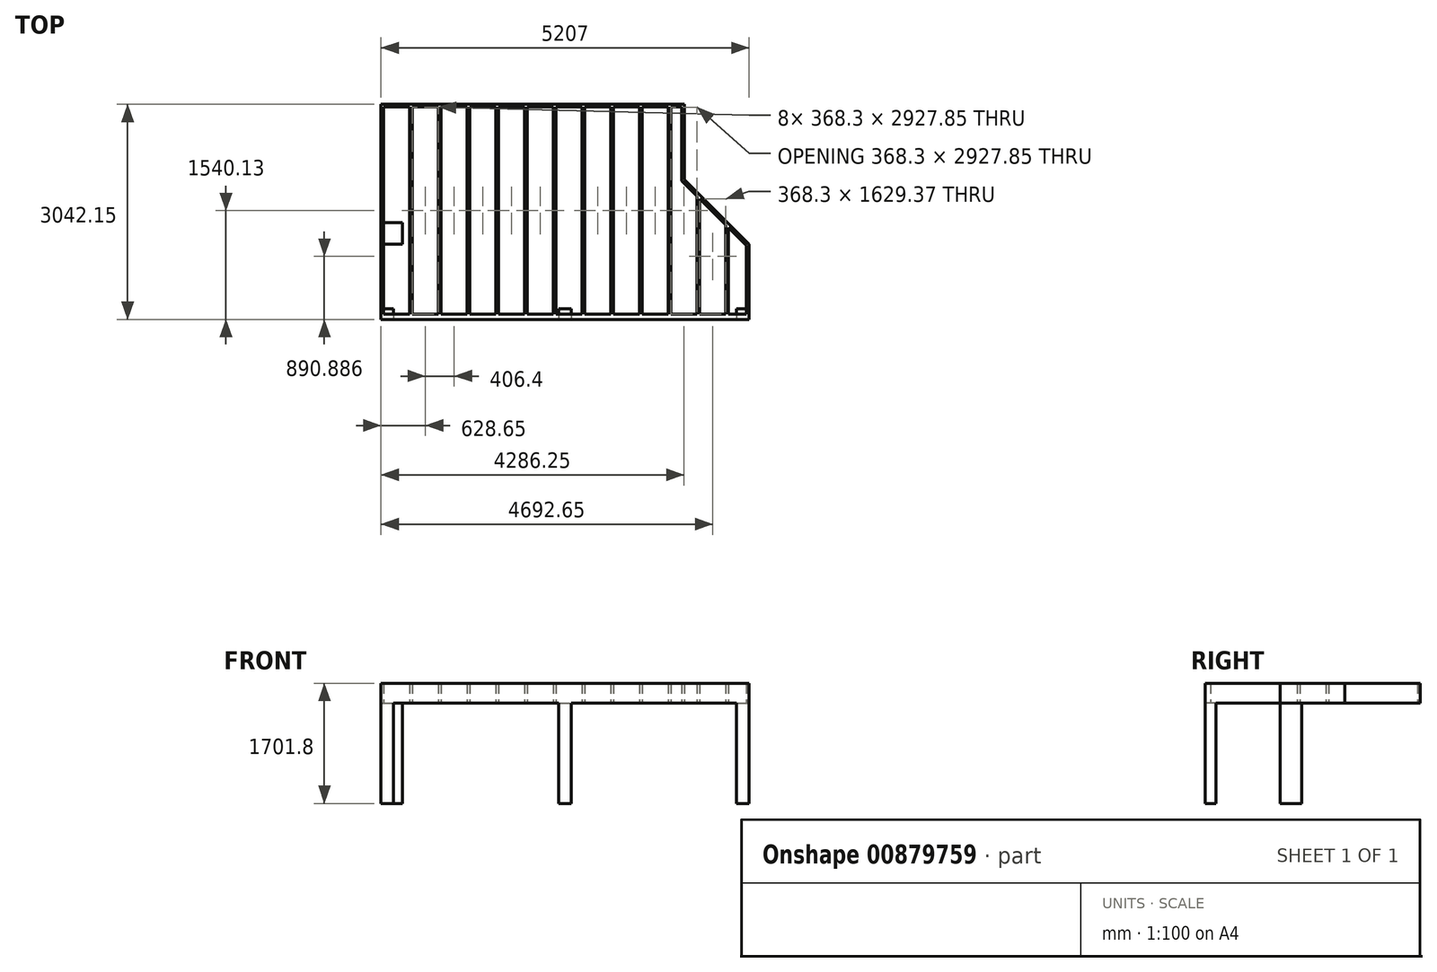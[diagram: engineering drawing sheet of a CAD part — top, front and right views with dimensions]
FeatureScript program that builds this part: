
annotation { "Feature Type Name" : "Feature", "Feature Type Description" : "" }
export const myFeature = defineFeature(function(context is Context, id is Id, definition is map)
    precondition{}
    {
        {
            var Q0;
            Q0=qCreatedBy(makeId("Top.planeOp"),FACE);
            var sketch = newSketch(context, id + "F0", { "sketchPlane" : qUnion([Q0])});
            skLineSegment(sketch, "E0.bottom", {"start": v(0, -1676.4) * mm, "end": v(304.8, -1676.4) * mm});
            skLineSegment(sketch, "E0.top", {"start": v(0, -1981.2) * mm, "end": v(304.8, -1981.2) * mm});
            skLineSegment(sketch, "E0.left", {"start": v(0, -1676.4) * mm, "end": v(0, -1981.2) * mm});
            skLineSegment(sketch, "E0.right", {"start": v(304.8, -1676.4) * mm, "end": v(304.8, -1981.2) * mm});
            skLineSegment(sketch, "E1.bottom", {"start": v(0, -2889.75) * mm, "end": v(177.8, -2889.75) * mm});
            skLineSegment(sketch, "E1.top", {"start": v(0, -3042.15) * mm, "end": v(177.8, -3042.15) * mm});
            skLineSegment(sketch, "E1.left", {"start": v(0, -2889.75) * mm, "end": v(0, -3042.15) * mm});
            skLineSegment(sketch, "E1.right", {"start": v(177.8, -2889.75) * mm, "end": v(177.8, -3042.15) * mm});
            skLineSegment(sketch, "E2.bottom", {"start": v(2514.6, -2889.75) * mm, "end": v(2692.4, -2889.75) * mm});
            skLineSegment(sketch, "E2.top", {"start": v(2514.6, -3042.15) * mm, "end": v(2692.4, -3042.15) * mm});
            skLineSegment(sketch, "E2.left", {"start": v(2514.6, -2889.75) * mm, "end": v(2514.6, -3042.15) * mm});
            skLineSegment(sketch, "E2.right", {"start": v(2692.4, -2889.75) * mm, "end": v(2692.4, -3042.15) * mm});
            skLineSegment(sketch, "E3.bottom", {"start": v(5029.2, -2889.75) * mm, "end": v(5207, -2889.75) * mm});
            skLineSegment(sketch, "E3.top", {"start": v(5029.2, -3042.15) * mm, "end": v(5207, -3042.15) * mm});
            skLineSegment(sketch, "E3.left", {"start": v(5029.2, -2889.75) * mm, "end": v(5029.2, -3042.15) * mm});
            skLineSegment(sketch, "E3.right", {"start": v(5207, -2889.75) * mm, "end": v(5207, -3042.15) * mm});
            skLineSegment(sketch, "E4", {"start": v(0, 0) * mm, "end": v(4292.6, 0) * mm, "construction": true});
            skLineSegment(sketch, "E5", {"start": v(4292.6, 0) * mm, "end": v(4292.6, -1066.8) * mm, "construction": true});
            skLineSegment(sketch, "E6", {"start": v(4292.6, -1066.8) * mm, "end": v(5226.55, -2000.75) * mm, "construction": true});
            skLineSegment(sketch, "E7", {"start": v(5226.55, -2000.75) * mm, "end": v(7106.15, -2000.75) * mm, "construction": true});
            skSolve(sketch);
        }
        {
            var Q0;
            Q0=qSketchRegion(id+"F0",true);
            extrude(context, id + "F1", {"entities" : qUnion([Q0]), "depth" : 1422.4 * mm, "offsetDistance" : 25.4 * mm});
        }
        {
            var Q0;
            Q0=makeQuery(id+"F1.opExtrude","CAP_FACE",FACE,{"disambiguationData":[OSD([sQuery(id+"F0.wireOp",EDGE,"E0.bottom"),sQuery(id+"F0.wireOp",EDGE,"E0.top"),sQuery(id+"F0.wireOp",EDGE,"E0.left"),sQuery(id+"F0.wireOp",EDGE,"E0.right")])],"isStart":false});
            var sketch = newSketch(context, id + "F2", { "sketchPlane" : qUnion([Q0])});
            skLineSegment(sketch, "E8.0", {"start": v(0, 0) * mm, "end": v(4292.6, 0) * mm});
            skLineSegment(sketch, "E9.0", {"start": v(4292.6, 0) * mm, "end": v(4292.6, -1066.8) * mm});
            skLineSegment(sketch, "E9.1", {"start": v(4292.6, -1066.8) * mm, "end": v(5207, -1981.2) * mm});
            skLineSegment(sketch, "E10", {"start": v(0, 0) * mm, "end": v(0, -3042.15) * mm});
            skLineSegment(sketch, "E11", {"start": v(0, -3042.15) * mm, "end": v(5207, -3042.15) * mm});
            skLineSegment(sketch, "E12", {"start": v(5207, -3042.15) * mm, "end": v(5207, -1981.2) * mm});
            skPoint(sketch, "E13.orphan", {"position": v(5226.55, -2000.75) * mm});
            skLineSegment(sketch, "E14.0", {"start": v(4254.5, -38.1) * mm, "end": v(4254.5, -1082.58) * mm});
            skLineSegment(sketch, "E14.1", {"start": v(5168.9, -3004.05) * mm, "end": v(5168.9, -1996.98) * mm});
            skLineSegment(sketch, "E14.2", {"start": v(38.1, -3004.05) * mm, "end": v(5168.9, -3004.05) * mm});
            skLineSegment(sketch, "E14.3", {"start": v(4254.5, -1082.58) * mm, "end": v(5168.9, -1996.98) * mm});
            skLineSegment(sketch, "E14.4", {"start": v(38.1, -38.1) * mm, "end": v(38.1, -3004.05) * mm});
            skLineSegment(sketch, "E14.5", {"start": v(38.1, -38.1) * mm, "end": v(4254.5, -38.1) * mm});
            skSolve(sketch);
        }
        {
            var Q0;
            Q0=qSketchRegion(id+"F2",true);
            extrude(context, id + "F3", {"entities" : qUnion([Q0]), "operationType" : NewBodyOperationType.ADD, "depth" : 279.4 * mm, "offsetDistance" : 25.4 * mm});
        }
        {
            var Q0;
            Q0=makeQuery(id+"F1.opExtrude","CAP_FACE",FACE,{"disambiguationData":[OSD([sQuery(id+"F0.wireOp",EDGE,"E1.bottom"),sQuery(id+"F0.wireOp",EDGE,"E1.top"),sQuery(id+"F0.wireOp",EDGE,"E1.left"),sQuery(id+"F0.wireOp",EDGE,"E1.right")])],"isStart":false});
            var sketch = newSketch(context, id + "F4", { "sketchPlane" : qUnion([Q0])});
            skPoint(sketch, "E15.oppositeSnap0", {"position": v(38.1, -2965.95) * mm});
            skLineSegment(sketch, "E15.bottom", {"start": v(38.1, -3004.05) * mm, "end": v(5168.9, -3004.05) * mm});
            skLineSegment(sketch, "E15.top", {"start": v(38.1, -2965.95) * mm, "end": v(5168.9, -2965.95) * mm});
            skLineSegment(sketch, "E15.left", {"start": v(38.1, -3004.05) * mm, "end": v(38.1, -2965.95) * mm});
            skLineSegment(sketch, "E15.right", {"start": v(5168.9, -3004.05) * mm, "end": v(5168.9, -2965.95) * mm});
            skSolve(sketch);
        }
        {
            var Q0;
            Q0=qSketchRegion(id+"F4",true);
            var Q1;
            Q1=makeQuery(id+"F3.opExtrude","CAP_FACE",FACE,{"disambiguationData":[OSD([sQuery(id+"F2.wireOp",EDGE,"E8.0"),sQuery(id+"F2.wireOp",EDGE,"E9.0"),sQuery(id+"F2.wireOp",EDGE,"E9.1"),sQuery(id+"F2.wireOp",EDGE,"E10"),sQuery(id+"F2.wireOp",EDGE,"E11"),sQuery(id+"F2.wireOp",EDGE,"E12"),sQuery(id+"F2.wireOp",EDGE,"E14.0"),sQuery(id+"F2.wireOp",EDGE,"E14.1"),sQuery(id+"F2.wireOp",EDGE,"E14.2"),sQuery(id+"F2.wireOp",EDGE,"E14.3"),sQuery(id+"F2.wireOp",EDGE,"E14.4"),sQuery(id+"F2.wireOp",EDGE,"E14.5")])],"isStart":false});
            extrude(context, id + "F5", {"entities" : qUnion([Q0]), "operationType" : NewBodyOperationType.ADD, "endBound" : BoundingType.UP_TO_SURFACE, "depth" : 25.4 * mm, "endBoundEntityFace" : qUnion([Q1]), "offsetDistance" : 25.4 * mm});
        }
        {
            var Q0;
            Q0=makeQuery(id+"F1.opExtrude","CAP_FACE",FACE,{"disambiguationData":[OSD([sQuery(id+"F0.wireOp",EDGE,"E0.bottom"),sQuery(id+"F0.wireOp",EDGE,"E0.top"),sQuery(id+"F0.wireOp",EDGE,"E0.left"),sQuery(id+"F0.wireOp",EDGE,"E0.right")])],"isStart":false});
            var sketch = newSketch(context, id + "F6", { "sketchPlane" : qUnion([Q0])});
            skLineSegment(sketch, "E16.bottom", {"start": v(406.4, -38.1) * mm, "end": v(444.5, -38.1) * mm});
            skLineSegment(sketch, "E16.top", {"start": v(406.4, -2965.95) * mm, "end": v(444.5, -2965.95) * mm});
            skLineSegment(sketch, "E16.left", {"start": v(406.4, -38.1) * mm, "end": v(406.4, -2965.95) * mm});
            skLineSegment(sketch, "E16.right", {"start": v(444.5, -38.1) * mm, "end": v(444.5, -2965.95) * mm});
            skLineSegment(sketch, "E17.1.0.0", {"start": v(850.9, -38.1) * mm, "end": v(850.9, -2965.95) * mm});
            skLineSegment(sketch, "E17.1.0.1", {"start": v(812.8, -38.1) * mm, "end": v(812.8, -2965.95) * mm});
            skLineSegment(sketch, "E17.1.0.2", {"start": v(812.8, -38.1) * mm, "end": v(850.9, -38.1) * mm});
            skLineSegment(sketch, "E17.1.0.3", {"start": v(812.8, -2965.95) * mm, "end": v(850.9, -2965.95) * mm});
            skLineSegment(sketch, "E17.2.0.0", {"start": v(1257.3, -38.1) * mm, "end": v(1257.3, -2965.95) * mm});
            skLineSegment(sketch, "E17.2.0.1", {"start": v(1219.2, -38.1) * mm, "end": v(1219.2, -2965.95) * mm});
            skLineSegment(sketch, "E17.2.0.2", {"start": v(1219.2, -38.1) * mm, "end": v(1257.3, -38.1) * mm});
            skLineSegment(sketch, "E17.2.0.3", {"start": v(1219.2, -2965.95) * mm, "end": v(1257.3, -2965.95) * mm});
            skLineSegment(sketch, "E17.3.0.0", {"start": v(1663.7, -38.1) * mm, "end": v(1663.7, -2965.95) * mm});
            skLineSegment(sketch, "E17.3.0.1", {"start": v(1625.6, -38.1) * mm, "end": v(1625.6, -2965.95) * mm});
            skLineSegment(sketch, "E17.3.0.2", {"start": v(1625.6, -38.1) * mm, "end": v(1663.7, -38.1) * mm});
            skLineSegment(sketch, "E17.3.0.3", {"start": v(1625.6, -2965.95) * mm, "end": v(1663.7, -2965.95) * mm});
            skLineSegment(sketch, "E17.4.0.0", {"start": v(2070.1, -38.1) * mm, "end": v(2070.1, -2965.95) * mm});
            skLineSegment(sketch, "E17.4.0.1", {"start": v(2032, -38.1) * mm, "end": v(2032, -2965.95) * mm});
            skLineSegment(sketch, "E17.4.0.2", {"start": v(2032, -38.1) * mm, "end": v(2070.1, -38.1) * mm});
            skLineSegment(sketch, "E17.4.0.3", {"start": v(2032, -2965.95) * mm, "end": v(2070.1, -2965.95) * mm});
            skLineSegment(sketch, "E17.5.0.0", {"start": v(2476.5, -38.1) * mm, "end": v(2476.5, -2965.95) * mm});
            skLineSegment(sketch, "E17.5.0.1", {"start": v(2438.4, -38.1) * mm, "end": v(2438.4, -2965.95) * mm});
            skLineSegment(sketch, "E17.5.0.2", {"start": v(2438.4, -38.1) * mm, "end": v(2476.5, -38.1) * mm});
            skLineSegment(sketch, "E17.5.0.3", {"start": v(2438.4, -2965.95) * mm, "end": v(2476.5, -2965.95) * mm});
            skLineSegment(sketch, "E17.6.0.0", {"start": v(2882.9, -38.1) * mm, "end": v(2882.9, -2965.95) * mm});
            skLineSegment(sketch, "E17.6.0.1", {"start": v(2844.8, -38.1) * mm, "end": v(2844.8, -2965.95) * mm});
            skLineSegment(sketch, "E17.6.0.2", {"start": v(2844.8, -38.1) * mm, "end": v(2882.9, -38.1) * mm});
            skLineSegment(sketch, "E17.6.0.3", {"start": v(2844.8, -2965.95) * mm, "end": v(2882.9, -2965.95) * mm});
            skLineSegment(sketch, "E17.7.0.0", {"start": v(3289.3, -38.1) * mm, "end": v(3289.3, -2965.95) * mm});
            skLineSegment(sketch, "E17.7.0.1", {"start": v(3251.2, -38.1) * mm, "end": v(3251.2, -2965.95) * mm});
            skLineSegment(sketch, "E17.7.0.2", {"start": v(3251.2, -38.1) * mm, "end": v(3289.3, -38.1) * mm});
            skLineSegment(sketch, "E17.7.0.3", {"start": v(3251.2, -2965.95) * mm, "end": v(3289.3, -2965.95) * mm});
            skLineSegment(sketch, "E17.8.0.0", {"start": v(3695.7, -38.1) * mm, "end": v(3695.7, -2965.95) * mm});
            skLineSegment(sketch, "E17.8.0.1", {"start": v(3657.6, -38.1) * mm, "end": v(3657.6, -2965.95) * mm});
            skLineSegment(sketch, "E17.8.0.2", {"start": v(3657.6, -38.1) * mm, "end": v(3695.7, -38.1) * mm});
            skLineSegment(sketch, "E17.8.0.3", {"start": v(3657.6, -2965.95) * mm, "end": v(3695.7, -2965.95) * mm});
            skLineSegment(sketch, "E17.9.0.0", {"start": v(4102.1, -38.1) * mm, "end": v(4102.1, -2965.95) * mm});
            skLineSegment(sketch, "E17.9.0.1", {"start": v(4064, -38.1) * mm, "end": v(4064, -2965.95) * mm});
            skLineSegment(sketch, "E17.9.0.2", {"start": v(4064, -38.1) * mm, "end": v(4102.1, -38.1) * mm});
            skLineSegment(sketch, "E17.9.0.3", {"start": v(4064, -2965.95) * mm, "end": v(4102.1, -2965.95) * mm});
            skLineSegment(sketch, "E17.direction1", {"start": v(406.4, -2965.95) * mm, "end": v(812.8, -2965.95) * mm, "construction": true});
            skLineSegment(sketch, "E18.top", {"start": v(4470.4, -2965.95) * mm, "end": v(4508.5, -2965.95) * mm});
            skLineSegment(sketch, "E18.left", {"start": v(4470.4, -1298.48) * mm, "end": v(4470.4, -2965.95) * mm});
            skLineSegment(sketch, "E18.right", {"start": v(4508.5, -1336.58) * mm, "end": v(4508.5, -2965.95) * mm});
            skLineSegment(sketch, "E19.top", {"start": v(4876.8, -2965.95) * mm, "end": v(4914.9, -2965.95) * mm});
            skLineSegment(sketch, "E19.left", {"start": v(4876.8, -1704.88) * mm, "end": v(4876.8, -2965.95) * mm});
            skLineSegment(sketch, "E19.right", {"start": v(4914.9, -1742.98) * mm, "end": v(4914.9, -2965.95) * mm});
            skLineSegment(sketch, "E20", {"start": v(4470.4, -1298.48) * mm, "end": v(4508.5, -1336.58) * mm});
            skLineSegment(sketch, "E21.trimOffspring", {"start": v(4876.8, -1704.88) * mm, "end": v(4914.9, -1742.98) * mm});
            skSolve(sketch);
        }
        {
            var Q0;
            Q0=qSketchRegion(id+"F6",true);
            var Q1;
            {var subQ0=sQuery(id+"F2.wireOp",EDGE,"E14.5");var subQ1=sQuery(id+"F2.wireOp",EDGE,"E14.4");var subQ2=sQuery(id+"F2.wireOp",EDGE,"E14.3");var subQ3=sQuery(id+"F2.wireOp",EDGE,"E14.2");var subQ4=sQuery(id+"F2.wireOp",EDGE,"E14.1");var subQ5=sQuery(id+"F2.wireOp",EDGE,"E14.0");var subQ6=sQuery(id+"F2.wireOp",EDGE,"E12");var subQ7=sQuery(id+"F2.wireOp",EDGE,"E11");var subQ8=sQuery(id+"F2.wireOp",EDGE,"E10");var subQ9=sQuery(id+"F2.wireOp",EDGE,"E9.1");var subQ10=sQuery(id+"F2.wireOp",EDGE,"E9.0");var subQ11=sQuery(id+"F2.wireOp",EDGE,"E8.0");Q1=makeQuery(id+"F5.boolean.opBoolean","MERGE",FACE,{"derivedFrom":[makeQuery(id+"F3.opExtrude","CAP_FACE",FACE,{"disambiguationData":[OSD([subQ11,subQ10,subQ9,subQ8,subQ7,subQ6,subQ5,subQ4,subQ3,subQ2,subQ1,subQ0])],"isStart":false}),makeQuery(id+"F5.opExtrude","CAP_FACE",FACE,{"disambiguationData":[OSD([subQ11,subQ10,subQ9,subQ8,subQ7,subQ6,subQ5,subQ4,subQ3,subQ2,subQ1,subQ0])],"isStart":false})]});}
            extrude(context, id + "F7", {"entities" : qUnion([Q0]), "operationType" : NewBodyOperationType.ADD, "endBound" : BoundingType.UP_TO_SURFACE, "depth" : 25.4 * mm, "endBoundEntityFace" : qUnion([Q1]), "offsetDistance" : 25.4 * mm});
        }
    });
